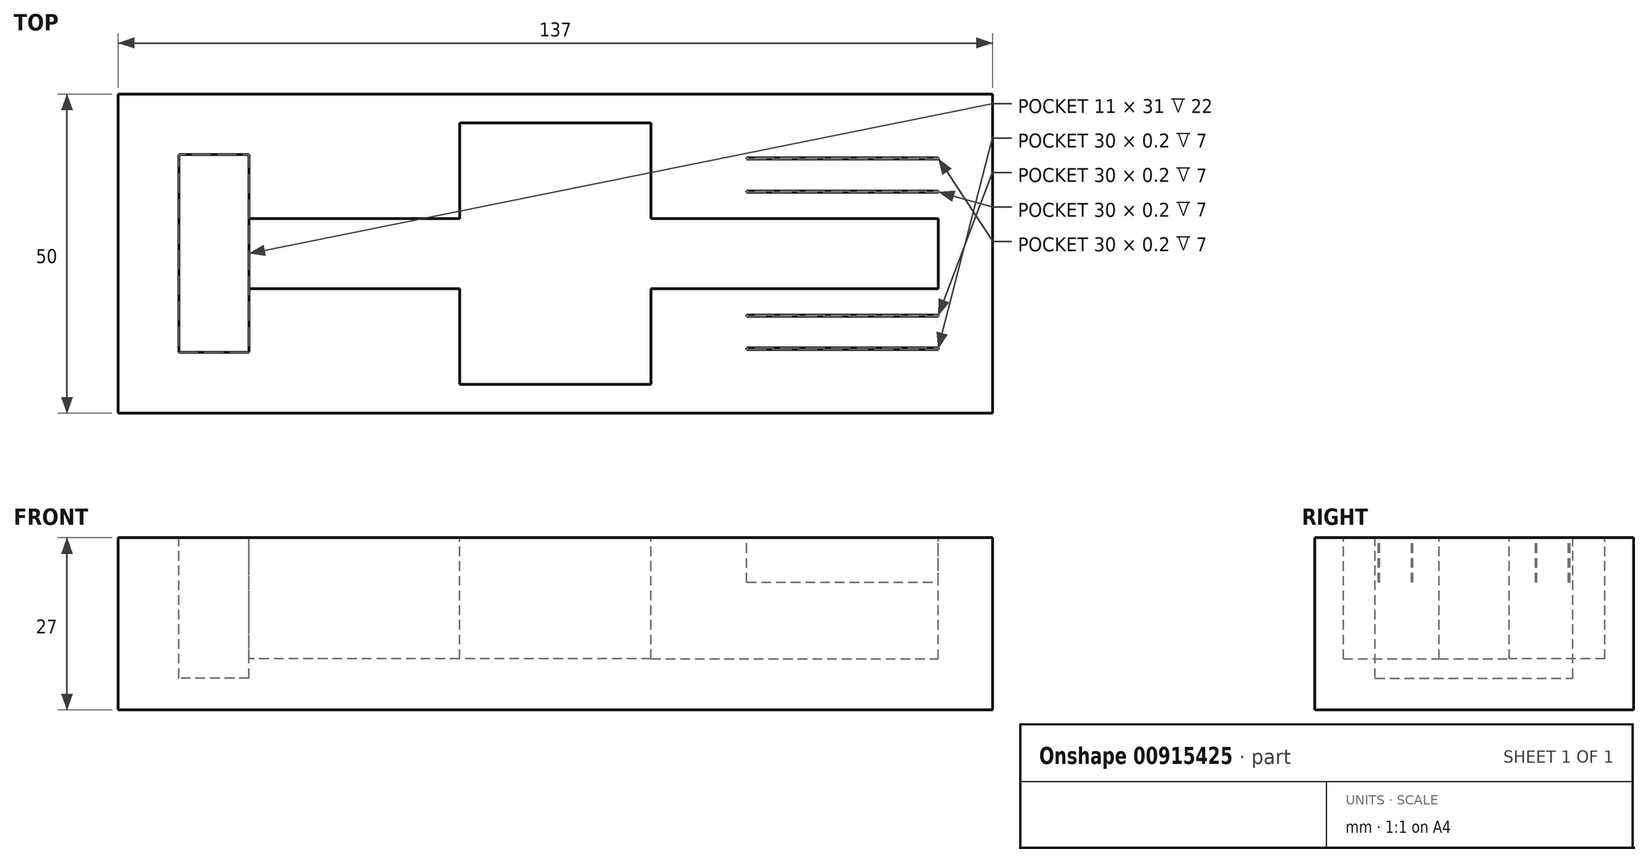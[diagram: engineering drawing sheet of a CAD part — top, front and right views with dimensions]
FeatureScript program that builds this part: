
annotation { "Feature Type Name" : "Feature", "Feature Type Description" : "" }
export const myFeature = defineFeature(function(context is Context, id is Id, definition is map)
    precondition{}
    {
        {
            var Q0;
            Q0=qCreatedBy(makeId("Top.planeOp"),FACE);
            var sketch = newSketch(context, id + "F0", { "sketchPlane" : qUnion([Q0])});
            skLineSegment(sketch, "E0.bottom", {"start": v(0, 0) * mm, "end": v(137, 0) * mm});
            skLineSegment(sketch, "E0.top", {"start": v(0, 50) * mm, "end": v(137, 50) * mm});
            skLineSegment(sketch, "E0.left", {"start": v(0, 0) * mm, "end": v(0, 50) * mm});
            skLineSegment(sketch, "E0.right", {"start": v(137, 0) * mm, "end": v(137, 50) * mm});
            skSolve(sketch);
        }
        {
            var Q0;
            Q0=makeQuery(id+"F0.imprint","IMPRINT",FACE,{"disambiguationData":[TD([[makeQuery(id+"F0.imprint","IMPRINT",EDGE,{"derivedFrom":sQuery(id+"F0.wireOp",EDGE,"E0.bottom")}),1.0]])]});
            extrude(context, id + "F1", {"entities" : qUnion([Q0]), "depth" : 27 * mm, "offsetDistance" : 25 * mm});
        }
        {
            var Q0;
            Q0=makeQuery(id+"F1.opExtrude","CAP_FACE",FACE,{"disambiguationData":[OSD([sQuery(id+"F0.wireOp",EDGE,"E0.bottom"),sQuery(id+"F0.wireOp",EDGE,"E0.top"),sQuery(id+"F0.wireOp",EDGE,"E0.left"),sQuery(id+"F0.wireOp",EDGE,"E0.right")])],"isStart":false});
            var sketch = newSketch(context, id + "F2", { "sketchPlane" : qUnion([Q0])});
            skLineSegment(sketch, "E1", {"start": v(9.5, 40.5) * mm, "end": v(9.5, 9.5) * mm});
            skLineSegment(sketch, "E2", {"start": v(9.5, 9.5) * mm, "end": v(20.5, 9.5) * mm});
            skLineSegment(sketch, "E3", {"start": v(20.5, 9.5) * mm, "end": v(20.5, 19.5) * mm});
            skLineSegment(sketch, "E4", {"start": v(20.5, 19.5) * mm, "end": v(128.5, 19.5) * mm});
            skLineSegment(sketch, "E5", {"start": v(128.5, 19.5) * mm, "end": v(128.5, 30.5) * mm});
            skLineSegment(sketch, "E6", {"start": v(128.5, 30.5) * mm, "end": v(20.5, 30.5) * mm});
            skLineSegment(sketch, "E7", {"start": v(20.5, 30.5) * mm, "end": v(20.5, 40.5) * mm});
            skLineSegment(sketch, "E8", {"start": v(20.5, 40.5) * mm, "end": v(9.5, 40.5) * mm});
            skSolve(sketch);
        }
        {
            var Q0;
            Q0 = qSketchRegion(id + "F2", true);
            extrude(context, id + "F3", {"entities" : qUnion([Q0]), "operationType" : NewBodyOperationType.REMOVE, "oppositeDirection" : true, "depth" : 22 * mm, "offsetDistance" : 25 * mm});
        }
        {
            var Q0;
            Q0=makeQuery(id+"F1.opExtrude","CAP_FACE",FACE,{"disambiguationData":[OSD([sQuery(id+"F0.wireOp",EDGE,"E0.bottom"),sQuery(id+"F0.wireOp",EDGE,"E0.top"),sQuery(id+"F0.wireOp",EDGE,"E0.left"),sQuery(id+"F0.wireOp",EDGE,"E0.right")])],"isStart":false});
            var sketch = newSketch(context, id + "F4", { "sketchPlane" : qUnion([Q0])});
            skLineSegment(sketch, "E9.bottom", {"start": v(53.5, 30.5) * mm, "end": v(83.5, 30.5) * mm});
            skLineSegment(sketch, "E9.top", {"start": v(53.5, 45.5) * mm, "end": v(83.5, 45.5) * mm});
            skLineSegment(sketch, "E9.left", {"start": v(53.5, 30.5) * mm, "end": v(53.5, 45.5) * mm});
            skLineSegment(sketch, "E9.right", {"start": v(83.5, 30.5) * mm, "end": v(83.5, 45.5) * mm});
            skLineSegment(sketch, "E10.bottom", {"start": v(53.5, 19.5) * mm, "end": v(83.5, 19.5) * mm});
            skLineSegment(sketch, "E10.top", {"start": v(53.5, 4.5) * mm, "end": v(83.5, 4.5) * mm});
            skLineSegment(sketch, "E10.left", {"start": v(53.5, 19.5) * mm, "end": v(53.5, 4.5) * mm});
            skLineSegment(sketch, "E10.right", {"start": v(83.5, 19.5) * mm, "end": v(83.5, 4.5) * mm});
            skSolve(sketch);
        }
        {
            var Q0;
            Q0 = qSketchRegion(id + "F4", true);
            extrude(context, id + "F5", {"entities" : qUnion([Q0]), "operationType" : NewBodyOperationType.REMOVE, "oppositeDirection" : true, "depth" : 22 * mm, "offsetDistance" : 25 * mm});
        }
        {
            var Q0;
            Q0=makeQuery(id+"F1.opExtrude","CAP_FACE",FACE,{"disambiguationData":[OSD([sQuery(id+"F0.wireOp",EDGE,"E0.bottom"),sQuery(id+"F0.wireOp",EDGE,"E0.top"),sQuery(id+"F0.wireOp",EDGE,"E0.left"),sQuery(id+"F0.wireOp",EDGE,"E0.right")])],"isStart":false});
            var sketch = newSketch(context, id + "F6", { "sketchPlane" : qUnion([Q0])});
            skLineSegment(sketch, "E11.bottom", {"start": v(98.5, 40) * mm, "end": v(128.5, 40) * mm});
            skLineSegment(sketch, "E11.top", {"start": v(98.5, 39.8) * mm, "end": v(128.5, 39.8) * mm});
            skLineSegment(sketch, "E11.left", {"start": v(98.5, 40) * mm, "end": v(98.5, 39.8) * mm});
            skLineSegment(sketch, "E11.right", {"start": v(128.5, 40) * mm, "end": v(128.5, 39.8) * mm});
            skLineSegment(sketch, "E12.bottom", {"start": v(98.5, 34.8) * mm, "end": v(128.5, 34.8) * mm});
            skLineSegment(sketch, "E12.top", {"start": v(98.5, 34.6) * mm, "end": v(128.5, 34.6) * mm});
            skLineSegment(sketch, "E12.left", {"start": v(98.5, 34.8) * mm, "end": v(98.5, 34.6) * mm});
            skLineSegment(sketch, "E12.right", {"start": v(128.5, 34.8) * mm, "end": v(128.5, 34.6) * mm});
            skLineSegment(sketch, "E13.bottom", {"start": v(98.5, 15.4) * mm, "end": v(128.5, 15.4) * mm});
            skLineSegment(sketch, "E13.top", {"start": v(98.5, 15.2) * mm, "end": v(128.5, 15.2) * mm});
            skLineSegment(sketch, "E13.left", {"start": v(98.5, 15.4) * mm, "end": v(98.5, 15.2) * mm});
            skLineSegment(sketch, "E13.right", {"start": v(128.5, 15.4) * mm, "end": v(128.5, 15.2) * mm});
            skLineSegment(sketch, "E14.bottom", {"start": v(98.5, 10.2) * mm, "end": v(128.5, 10.2) * mm});
            skLineSegment(sketch, "E14.top", {"start": v(98.5, 10) * mm, "end": v(128.5, 10) * mm});
            skLineSegment(sketch, "E14.left", {"start": v(98.5, 10.2) * mm, "end": v(98.5, 10) * mm});
            skLineSegment(sketch, "E14.right", {"start": v(128.5, 10.2) * mm, "end": v(128.5, 10) * mm});
            skSolve(sketch);
        }
        {
            var Q0;
            Q0 = qSketchRegion(id + "F6", true);
            extrude(context, id + "F7", {"entities" : qUnion([Q0]), "operationType" : NewBodyOperationType.REMOVE, "oppositeDirection" : true, "depth" : 7 * mm, "offsetDistance" : 25 * mm});
        }
        {
            var Q0;
            Q0=makeQuery(id+"F5.boolean.opBoolean","MERGE",FACE,{"derivedFrom":[makeQuery(id+"F3.boolean.opBoolean","COPY",FACE,{"derivedFrom":makeQuery(id+"F3.opExtrude","CAP_FACE",FACE,{"disambiguationData":[OSD([sQuery(id+"F2.wireOp",EDGE,"E1"),sQuery(id+"F2.wireOp",EDGE,"E2"),sQuery(id+"F2.wireOp",EDGE,"E3"),sQuery(id+"F2.wireOp",EDGE,"E4"),sQuery(id+"F2.wireOp",EDGE,"E5"),sQuery(id+"F2.wireOp",EDGE,"E6"),sQuery(id+"F2.wireOp",EDGE,"E7"),sQuery(id+"F2.wireOp",EDGE,"E8")])],"isStart":false})})],"fromTools":[makeQuery(id+"F5.opExtrude","CAP_FACE",FACE,{"disambiguationData":[OSD([sQuery(id+"F4.wireOp",EDGE,"jiHQ6TSW-eDgy-8g1j-mGGJ-k4yg5xf1hOWB.left"),sQuery(id+"F4.wireOp",EDGE,"jiHQ6TSW-eDgy-8g1j-mGGJ-k4yg5xf1hOWB.right"),sQuery(id+"F4.wireOp",EDGE,"G145XSz5-qBFS-OZZF-YrqA-IwbM2XwhraXx"),sQuery(id+"F4.wireOp",EDGE,"D197SGJM-4Nrk-KXMF-fEkl-HpU7m7OVNXr0")])],"isStart":false})]});
            var sketch = newSketch(context, id + "F8", { "sketchPlane" : qUnion([Q0])});
            skLineSegment(sketch, "E15.bottom", {"start": v(20.5, 47.09) * mm, "end": v(131.73, 47.09) * mm});
            skLineSegment(sketch, "E15.top", {"start": v(20.5, 3.18) * mm, "end": v(131.73, 3.18) * mm});
            skLineSegment(sketch, "E15.left", {"start": v(20.5, 47.09) * mm, "end": v(20.5, 3.18) * mm});
            skLineSegment(sketch, "E15.right", {"start": v(131.73, 47.09) * mm, "end": v(131.73, 3.18) * mm});
            skSolve(sketch);
        }
        {
            var Q0;
            Q0 = qSketchRegion(id + "F8", true);
            extrude(context, id + "F9", {"entities" : qUnion([Q0]), "operationType" : NewBodyOperationType.ADD, "depth" : 3 * mm, "offsetDistance" : 25 * mm});
        }
    });
